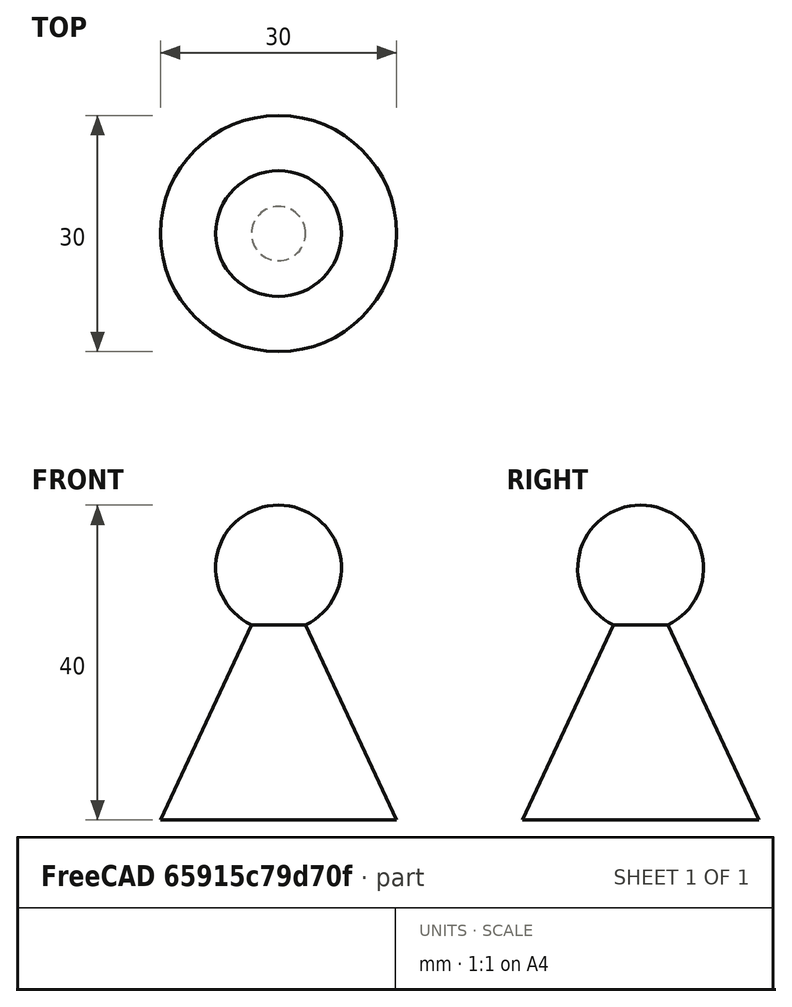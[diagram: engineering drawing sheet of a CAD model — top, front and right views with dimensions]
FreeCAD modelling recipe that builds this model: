
FCSTD DOCUMENT  (FreeCAD 0.21R33694 (Git))
Label: Solución Reto 5
License: All rights reserved
LicenseURL: http://en.wikipedia.org/wiki/All_rights_reserved
objects: Sketcher::SketchObject×1, PartDesign::Revolution×1, PartDesign::Body×1
note: 4 computed .brp shape members not serialized (recipe doc carries the construction recipe); baked Part::Feature solids carry a one-line shape summary decoded from their .brp

FEATURE [Sketcher::SketchObject] Sketch
  FullyConstrained = true
  MapMode = 5
  Placement = pos=(0,0,0) rot=(1,0,0;1.5708rad)
  Support = -> [XZ_Plane]
  sketch-geometry (4):
    g0: ArcOfCircle CenterX=0 CenterY=32 CenterZ=0 NormalX=0 NormalY=0 NormalZ=1 AngleXU=0 Radius=8 StartAngle=5.15758 EndAngle=7.85398
    g1: LineSegment StartX=2.4e-15 StartY=40 StartZ=0 EndX=0 EndY=0 EndZ=0
    g2: LineSegment StartX=0 StartY=0 StartZ=0 EndX=15 EndY=0 EndZ=0
    g3: LineSegment StartX=15 StartY=0 StartZ=0 EndX=3.44501 EndY=24.7798 EndZ=0
  constraints (13):
    c: PointOnObject(g0,g-2)
    c: PointOnObject(g0,g-2)
    c: Coincident(g0,g1)
    c: Coincident(g1,g2)
    c: PointOnObject(g2,g-1)
    c: Horizontal(g2)
    c: Coincident(g2,g3)
    c: Coincident(g3,g0)
    c: DistanceY(g1,g1) = 40
    c: DistanceX(g2,g2) = 15
    c: Angle(g3,g2) = 1.13446
    c: Parallel(g1,g-2)
    c: Radius(g0) = 8
FEATURE [PartDesign::Revolution] Revolution
  Angle = 360
  Axis = (0,2e-16,1)
  Base = (0,0,0)
  Placement = pos=(0,0,0) rot=(1,0,0;1.5708rad)
  Profile = -> Sketch
  ReferenceAxis = -> Sketch [V_Axis]
  Refine = true
  Reversed = true
FEATURE [PartDesign::Body] Body  label="Cuerpo"
  Group = -> [Sketch,Revolution]
  Origin = -> Origin
  Tip = -> Revolution
